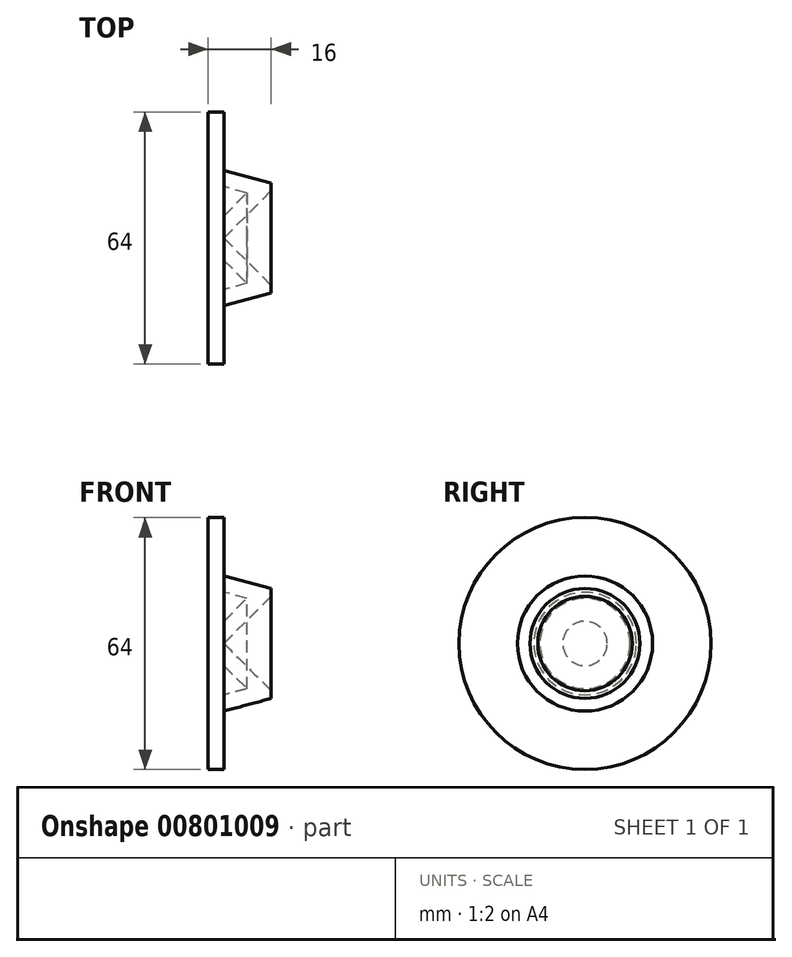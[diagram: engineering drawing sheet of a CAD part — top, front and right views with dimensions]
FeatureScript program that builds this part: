
annotation { "Feature Type Name" : "Feature", "Feature Type Description" : "" }
export const myFeature = defineFeature(function(context is Context, id is Id, definition is map)
    precondition{}
    {
        {
            var Q0;
            Q0=qCreatedBy(makeId("Top.planeOp"),FACE);
            var sketch = newSketch(context, id + "F0", { "sketchPlane" : qUnion([Q0])});
            skLineSegment(sketch, "E0", {"start": v(0, 0) * mm, "end": v(0, -32) * mm});
            skLineSegment(sketch, "E1", {"start": v(0, -32) * mm, "end": v(4, -32) * mm});
            skLineSegment(sketch, "E2", {"start": v(4, -32) * mm, "end": v(4, -22.83) * mm});
            skLineSegment(sketch, "E3", {"start": v(4, 0) * mm, "end": v(0, 0) * mm});
            skLineSegment(sketch, "E4", {"start": v(4, -5.66) * mm, "end": v(4, -13.03) * mm});
            skLineSegment(sketch, "E5", {"start": v(4, -13.03) * mm, "end": v(9.82, -11.47) * mm});
            skLineSegment(sketch, "E6", {"start": v(9.82, -11.47) * mm, "end": v(4, -5.66) * mm});
            skLineSegment(sketch, "E7", {"start": v(4, 0) * mm, "end": v(16, -12) * mm});
            skLineSegment(sketch, "E8", {"start": v(16, -12) * mm, "end": v(16, -13.96) * mm});
            skLineSegment(sketch, "E9", {"start": v(16, -13.96) * mm, "end": v(4, -17.17) * mm});
            skLineSegment(sketch, "E10", {"start": v(4, -17.17) * mm, "end": v(4, -22.83) * mm});
            skSolve(sketch);
        }
        {
            var Q0;
            Q0=makeQuery(id+"F0.imprint","IMPRINT",FACE,{"disambiguationData":[TD([[makeQuery(id+"F0.imprint","IMPRINT",EDGE,{"derivedFrom":sQuery(id+"F0.wireOp",EDGE,"E0")}),1.0]])]});
            var Q1;
            Q1=sQuery(id+"F0.wireOp",EDGE,"E3");
            revolve(context, id + "F1", {"surfaceOperationType" : NewSurfaceOperationType.NEW, "entities" : qUnion([Q0]), "axis" : qUnion([Q1]), "revolveType" : RevolveType.FULL});
        }
    });
